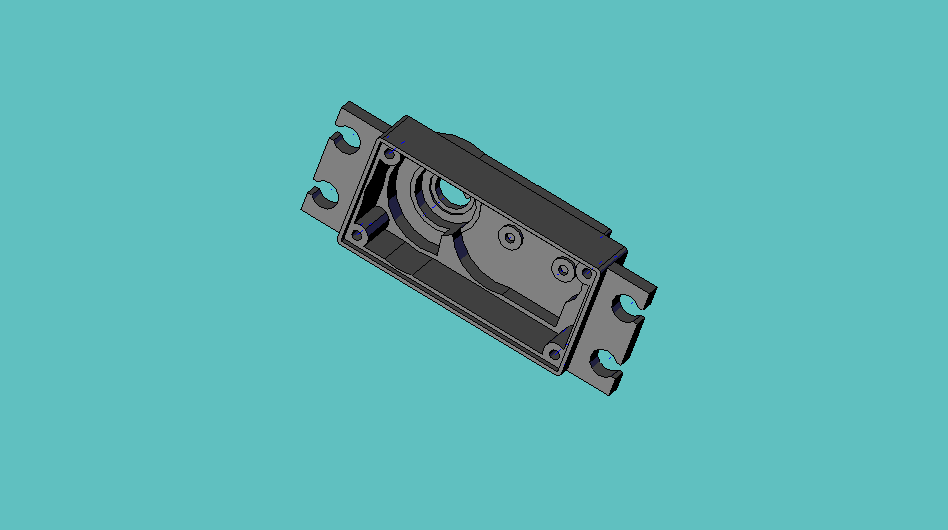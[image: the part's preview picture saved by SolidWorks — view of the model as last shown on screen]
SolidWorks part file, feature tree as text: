
SOLIDWORKS PART (.sldprt)
format: sldprt  version: not decoded by parser v0  size: 1,231,872 bytes
history: native  units: mm
features: sketch x23, extrude x13, cut_extrude x9, material x1, shell x1, plane x1, mirror x1 (+13 scaffold rows collapsed)
feature tree (62):
  scaffold x13  (default folders/planes/origin — collapsed)
  material  "ABS"
  sketch  "Sketch2"  dims[D3=0.762mm D1=38.735mm D2=19.685mm]
  extrude  "Extrude1"  Depth=8.255mm
  sketch  "Sketch4"  dims[D1=0.381mm]
  extrude  "Extrude2"  Depth=0.381mm
  sketch  "Sketch5"  dims[c1.D1=18.923mm c1.D5=0.381mm c1.D7=~5.845387mm c1.D4=5.5245mm c2.D1=37.211mm c2.D2=0.381mm c2.D3=0.381mm c2.D4=3.937mm c2.D6=7.62mm c2.D7=1.524mm c3.D4=20.574mm]
  extrude  "Extrude3"  Depth=2.54mm
  sketch  "Sketch7"  dims[D1=12.7mm]
  extrude  "Extrude4"  Depth=1.905mm
  sketch  "Sketch8"  dims[D1=9.906mm]
  extrude  "Extrude5"  Depth=0.381mm
  shell  "Shell1"  Thickness=1.27mm
  sketch  "Sketch9"  dims[D1=17.78mm]
  sketch  "Sketch28"  dims[D1=10.0mm]
  extrude  "Extrude14"  [1 undecoded]
  sketch  "Sketch10"  dims[D1=0.635mm]
  cut_extrude  "Cut-Extrude2"  Depth=0.889mm
  sketch  "Sketch12"  dims[c1.D5=3.81mm c1.Screw Hole From Sides=2.286mm c1.D2=2.54mm c1.D3=~2.160657mm c1.D4=~2.334903mm c2.D2=2.54mm]
  extrude  "Extrude6"  Depth=7.112mm
  cut_extrude  "Cut-Extrude3"  [1 undecoded]
  sketch  "Sketch13"  dims[D1=0.0mm]
  cut_extrude  "Cut-Extrude5"  Depth=0.381mm
  sketch  "Sketch14"  dims[D1=0.254mm]
  cut_extrude  "Cut-Extrude6"  Depth=6.35mm
  sketch  "Sketch16"  dims[c1.End Offset=0.381mm c1.D2=~1.971345mm c1.D1=2.413mm c2.D2=1.905mm]
  extrude  "Extrude7"  Depth=7.239mm
  sketch  "Sketch18"  dims[c1.D1=1.0922mm c1.D2=1.0922mm c2.D1=1.0922mm c2.D2=3.429mm]
  extrude  "Extrude8"  Depth=0.635mm
  sketch  "Sketch19"  dims[c1.D2=4.445mm c1.D1=2.54mm c2.D2=4.699mm c2.D3=~4.446343mm c2.D4=~4.446343mm c2.Flange Hole Offset=4.318mm c3.D4=~3.102159mm c3.D3=10.16mm]
  cut_extrude  "Cut-Extrude7"  [1 undecoded]
  sketch  "Sketch20"  dims[Hole Open Width=2.54mm D2=~1.697861mm]
  cut_extrude  "Cut-Extrude8"  Depth=2.54mm
  sketch  "Sketch21"
  plane  "Plane1"
  sketch  "Sketch22"  dims[c1.D2=16.51mm c1.D3=8.1915mm c1.D1=16.256mm c2.D3=33.782mm c2.D4=33.2994mm]
  extrude  "Extrude10"  Depth=2.54mm
  sketch  "Sketch23"
  cut_extrude  "Cut-Extrude10"  [1 undecoded]
  sketch  "Sketch24"  dims[D1=3.81mm]
  extrude  "Extrude11"  Depth=0.508mm
  sketch  "Sketch25"  dims[D1=1.5875mm]
  cut_extrude  "Cut-Extrude11"  Depth=0.762mm
  sketch  "Sketch26"  dims[D1=11.5316mm]
  extrude  "Extrude12"  Depth=0.0508mm
  sketch  "Sketch27"  dims[D3=0.381mm D2=12.7mm D1=0.0mm]
  extrude  "Extrude13"  Depth=0.127mm
  sketch  "Sketch29"  dims[D1=5.842mm]
  cut_extrude  "Cut-Extrude12"  [1 undecoded]
  mirror  "Mirror1"  Flange Hole Offset=4.318mm
decode coverage: 40 of 47 modeling features carry decoded parameters
note: ~ marks probable driven/reference dimensions
note: 5 parameter values undecoded
summary: no parameter record found for 5 features
note: suppression state not decoded; provenance and decode notes live in map.json
